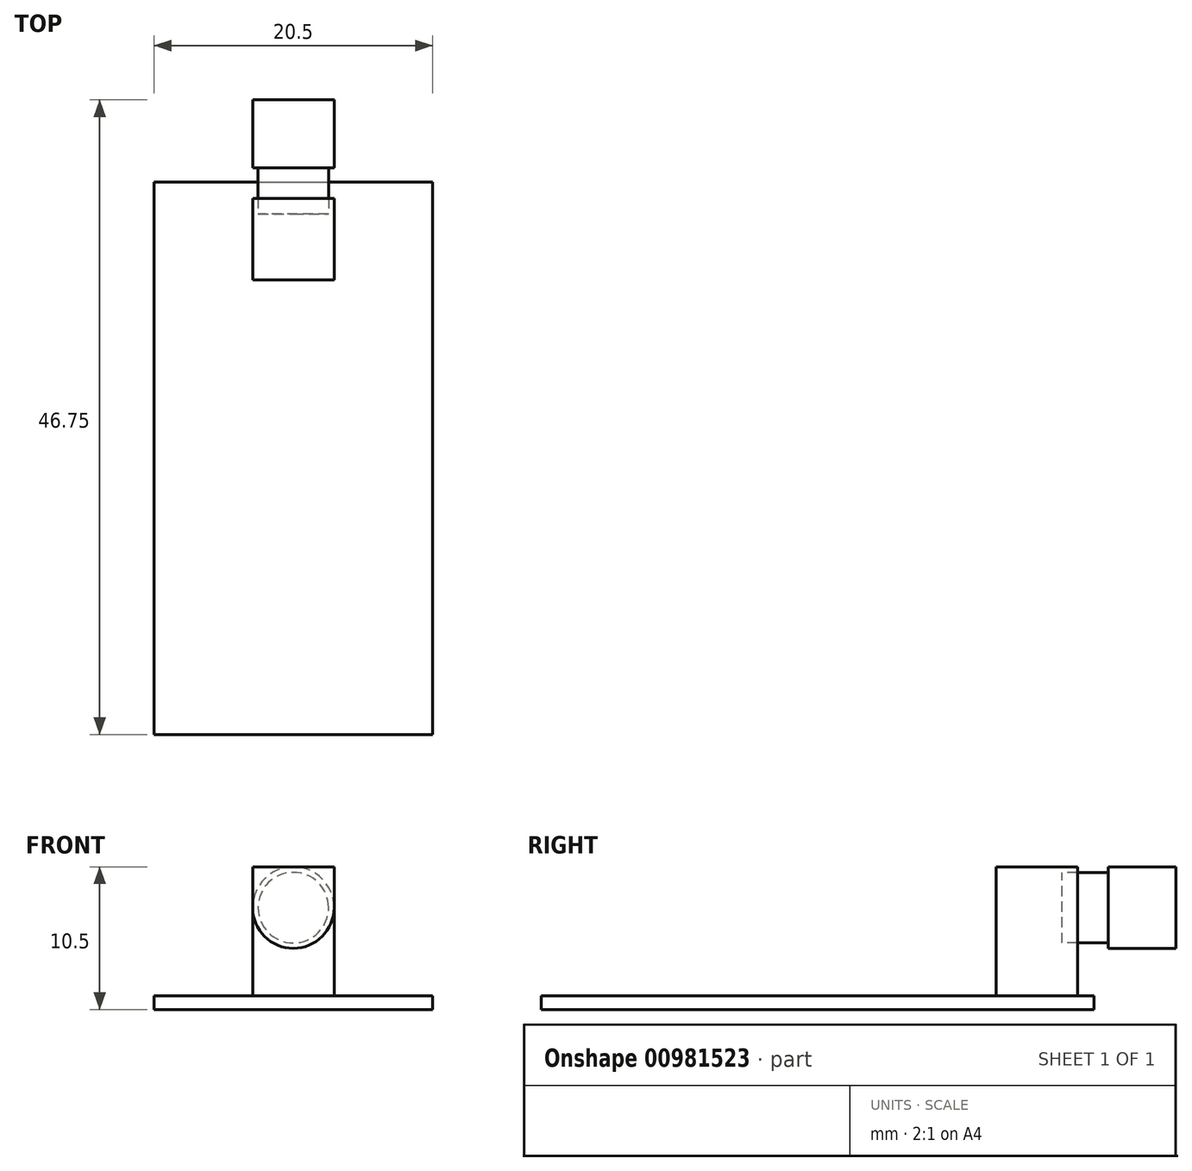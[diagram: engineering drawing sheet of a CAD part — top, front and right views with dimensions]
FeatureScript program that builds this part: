
annotation { "Feature Type Name" : "Feature", "Feature Type Description" : "" }
export const myFeature = defineFeature(function(context is Context, id is Id, definition is map)
    precondition{}
    {
        {
            var Q0;
            Q0=qCreatedBy(makeId("Top.planeOp"),FACE);
            var sketch = newSketch(context, id + "F0", { "sketchPlane" : qUnion([Q0])});
            skLineSegment(sketch, "E0.bottom", {"start": v(-10.25, 20.35) * mm, "end": v(10.25, 20.35) * mm});
            skLineSegment(sketch, "E0.top", {"start": v(-10.25, -20.35) * mm, "end": v(10.25, -20.35) * mm});
            skLineSegment(sketch, "E0.left", {"start": v(-10.25, 20.35) * mm, "end": v(-10.25, -20.35) * mm});
            skLineSegment(sketch, "E0.right", {"start": v(10.25, 20.35) * mm, "end": v(10.25, -20.35) * mm});
            skPoint(sketch, "E0.middle", {"position": v(0, 0) * mm});
            skLineSegment(sketch, "E1.bottom", {"start": v(-3, 19.15) * mm, "end": v(3, 19.15) * mm});
            skLineSegment(sketch, "E1.top", {"start": v(-3, 13.15) * mm, "end": v(3, 13.15) * mm});
            skLineSegment(sketch, "E1.left", {"start": v(-3, 19.15) * mm, "end": v(-3, 13.15) * mm});
            skLineSegment(sketch, "E1.right", {"start": v(3, 19.15) * mm, "end": v(3, 13.15) * mm});
            skPoint(sketch, "E1.middle", {"position": v(0, 16.15) * mm});
            skSolve(sketch);
        }
        {
            var Q0;
            Q0=makeQuery(id+"F0.imprint","IMPRINT",FACE,{"disambiguationData":[TD([[makeQuery(id+"F0.imprint","IMPRINT",EDGE,{"derivedFrom":sQuery(id+"F0.wireOp",EDGE,"E0.bottom")}),-1.0]])]});
            var Q1;
            Q1=makeQuery(id+"F0.imprint","IMPRINT",FACE,{"disambiguationData":[TD([[makeQuery(id+"F0.imprint","IMPRINT",EDGE,{"derivedFrom":sQuery(id+"F0.wireOp",EDGE,"E1.bottom")}),-1.0]])]});
            extrude(context, id + "F1", {"entities" : qUnion([Q0, Q1]), "depth" : 1 * mm, "offsetDistance" : 25 * mm});
        }
        {
            var Q0;
            Q0=makeQuery(id+"F0.imprint","IMPRINT",FACE,{"disambiguationData":[TD([[makeQuery(id+"F0.imprint","IMPRINT",EDGE,{"derivedFrom":sQuery(id+"F0.wireOp",EDGE,"E1.bottom")}),-1.0]])]});
            extrude(context, id + "F2", {"entities" : qUnion([Q0]), "operationType" : NewBodyOperationType.ADD, "depth" : 10.5 * mm, "offsetDistance" : 25 * mm});
        }
        {
            var Q0;
            Q0=qCreatedBy(makeId("Front.planeOp"),FACE);
            var sketch = newSketch(context, id + "F3", { "sketchPlane" : qUnion([Q0])});
            skCircle(sketch, "E2", {"center": v(0, 7.5) * mm, "radius": 2.6 * mm});
            skCircle(sketch, "E3", {"center": v(0, 7.5) * mm, "radius": 3 * mm});
            skSolve(sketch);
        }
        {
            var Q0;
            Q0=makeQuery(id+"F3.imprint","IMPRINT",FACE,{"disambiguationData":[TD([[makeQuery(id+"F3.imprint","IMPRINT",EDGE,{"derivedFrom":sQuery(id+"F3.wireOp",EDGE,"E2")}),1.0]])]});
            extrude(context, id + "F4", {"entities" : qUnion([Q0]), "oppositeDirection" : true, "depth" : 21.4 * mm, "offsetDistance" : 25 * mm, "hasSecondDirection" : true, "secondDirectionOppositeDirection" : true, "secondDirectionDepth" : 18 * mm});
        }
        {
            var Q0;
            Q0=makeQuery(id+"F3.imprint","IMPRINT",FACE,{"disambiguationData":[TD([[makeQuery(id+"F3.imprint","IMPRINT",EDGE,{"derivedFrom":sQuery(id+"F3.wireOp",EDGE,"E2")}),-1.0]])]});
            var Q1;
            Q1=makeQuery(id+"F3.imprint","IMPRINT",FACE,{"disambiguationData":[TD([[makeQuery(id+"F3.imprint","IMPRINT",EDGE,{"derivedFrom":sQuery(id+"F3.wireOp",EDGE,"E2")}),1.0]])]});
            extrude(context, id + "F5", {"entities" : qUnion([Q0, Q1]), "operationType" : NewBodyOperationType.ADD, "oppositeDirection" : true, "depth" : 26.4 * mm, "offsetDistance" : 25 * mm, "hasSecondDirection" : true, "secondDirectionOppositeDirection" : true, "secondDirectionDepth" : 21.4 * mm});
        }
    });
